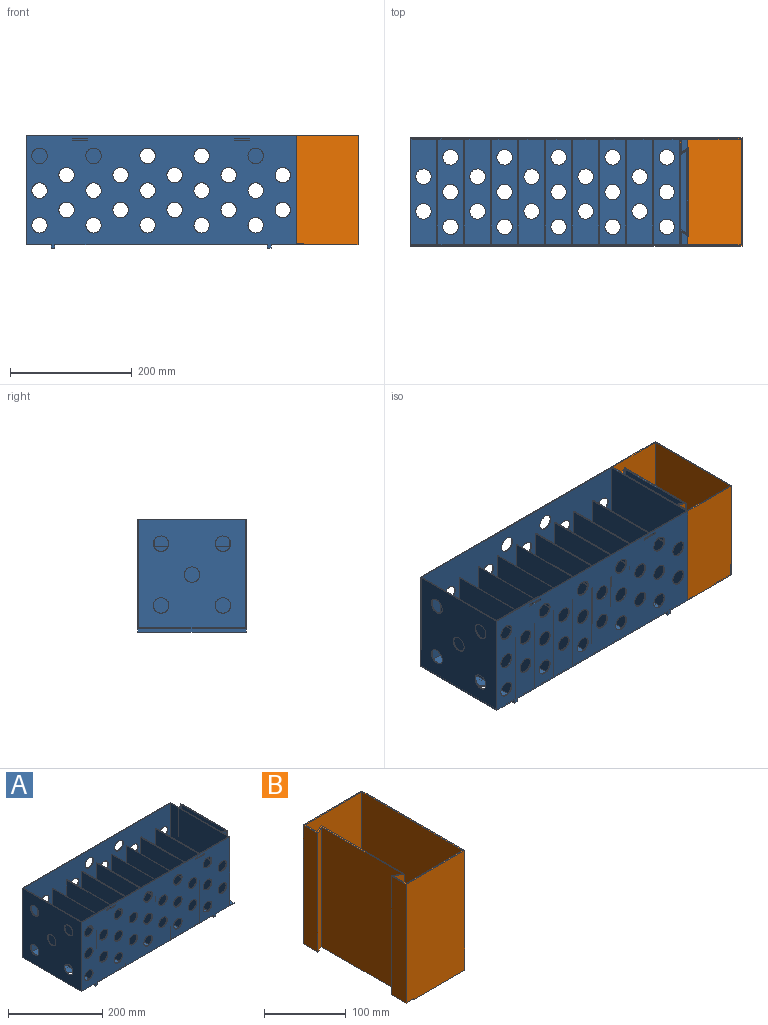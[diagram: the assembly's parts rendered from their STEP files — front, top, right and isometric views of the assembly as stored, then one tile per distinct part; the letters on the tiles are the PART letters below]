
ASSEMBLY  parts=2 mates=1
PART A: 151 faces, bbox 457.2x177.8x185.7 mm
  f0: plane 457.2x185.74mm, normal (0,-1,0), area 67009.6mm2, adj f20,f31,f32,f34,f59,f62,f63,f64
  f1: plane 441.33x177.8mm, normal (0,1,0), area 63733.4mm2, adj f2,f3,f4,f5,f6,f7,f8,f9
  f2: plane 174.63x133.35mm, normal (-1,0,0), area 23286.2mm2, adj f1,f61,f69,f134
  f3: plane 174.63x133.35mm, normal (-1,0,0), area 23286.2mm2, adj f1,f22,f69,f136
  f4: plane 174.63x133.35mm, normal (1,0,0), area 23286.2mm2, adj f1,f22,f69,f135
  f5: plane 174.63x133.35mm, normal (-1,0,0), area 23286.2mm2, adj f1,f23,f69,f138
  f6: plane 174.63x133.35mm, normal (1,0,0), area 23286.2mm2, adj f1,f23,f69,f137
  f7: plane 174.63x133.35mm, normal (-1,0,0), area 23286.2mm2, adj f1,f24,f69,f140
  f8: plane 174.63x133.35mm, normal (1,0,0), area 23286.2mm2, adj f1,f24,f69,f139
  f9: plane 174.63x133.35mm, normal (-1,0,0), area 23286.2mm2, adj f1,f25,f69,f142
  f10: plane 174.63x133.35mm, normal (1,0,0), area 23286.2mm2, adj f1,f25,f69,f141
  f11: plane 174.63x133.35mm, normal (1,0,0), area 23286.2mm2, adj f1,f26,f69,f142
  f12: plane 174.63x133.35mm, normal (-1,0,0), area 23286.2mm2, adj f1,f27,f69,f141
  f13: plane 174.63x133.35mm, normal (1,0,0), area 23286.2mm2, adj f1,f27,f69,f140
  f14: plane 174.63x133.35mm, normal (-1,0,0), area 23286.2mm2, adj f1,f28,f69,f139
  f15: plane 174.63x133.35mm, normal (1,0,0), area 23286.2mm2, adj f1,f28,f69,f138
  f16: plane 174.63x133.35mm, normal (-1,0,0), area 23286.2mm2, adj f1,f29,f69,f137
  f17: plane 174.63x133.35mm, normal (1,0,0), area 23286.2mm2, adj f1,f29,f69,f136
  f18: plane 174.63x133.35mm, normal (-1,0,0), area 23286.2mm2, adj f1,f30,f69,f135
  f19: plane 174.63x133.35mm, normal (1,0,0), area 23286.2mm2, adj f1,f30,f69,f134
  f20: plane 25.4x12.7mm, normal (0,0,1), area 282.3mm2, adj f0,f59,f76,f77
  f21: plane 25.4x12.7mm, normal (0,0,1), area 282.3mm2, adj f33,f59,f74,f75
  f22: plane 174.63x42.7mm, normal (0,0,1), area 6443.7mm2, adj f1,f3,f4,f36,f37,f69
  f23: plane 174.63x42.7mm, normal (0,0,1), area 6443.7mm2, adj f1,f5,f6,f38,f39,f69
  f24: plane 174.63x42.7mm, normal (0,0,1), area 6443.7mm2, adj f1,f7,f8,f40,f41,f69
  f25: plane 174.63x42.7mm, normal (0,0,1), area 6443.7mm2, adj f1,f9,f10,f42,f43,f69
  f26: plane 174.63x42.7mm, normal (0,0,1), area 5937mm2, adj f1,f11,f56,f57,f58,f69,f70
  f27: plane 174.63x42.7mm, normal (0,0,1), area 5937mm2, adj f1,f12,f13,f53,f54,f55,f69
  f28: plane 174.63x42.7mm, normal (0,0,1), area 5937mm2, adj f1,f14,f15,f50,f51,f52,f69
  f29: plane 174.63x42.7mm, normal (0,0,1), area 5937mm2, adj f1,f16,f17,f47,f48,f49,f69
  f30: plane 174.63x42.7mm, normal (0,0,1), area 5937mm2, adj f1,f18,f19,f44,f45,f46,f69
  f31: plane 349.25x177.8mm, normal (0,0,-1), area 51962.5mm2, adj f0,f33,f36,f37,f38,f39,f40,f41
  f32: plane 177.8x53.98mm, normal (0,0,-1), area 8076.6mm2, adj f0,f33,f56,f57,f58,f59,f64
  f33: plane 457.2x185.74mm, normal (0,1,0), area 68691mm2, adj f21,f31,f32,f34,f59,f62,f63,f64
  f34: plane 179.39x177.8mm, normal (-1,0,0), area 29361.6mm2, adj f0,f33,f62,f80,f129,f130,f131,f132
  f35: cylinder r=12.7mm len=25.4mm, axis (0,0,-1), area 126.7mm2, adj f61,f62
  f36: cylinder r=12.7mm len=25.4mm, axis (0,0,-1), area 126.7mm2, adj f22,f31
  f37: cylinder r=12.7mm len=25.4mm, axis (0,0,-1), area 126.7mm2, adj f22,f31
  f38: cylinder r=12.7mm len=25.4mm, axis (0,0,-1), area 126.7mm2, adj f23,f31
  f39: cylinder r=12.7mm len=25.4mm, axis (0,0,-1), area 126.7mm2, adj f23,f31
  f40: cylinder r=12.7mm len=25.4mm, axis (0,0,-1), area 126.7mm2, adj f24,f31
  f41: cylinder r=12.7mm len=25.4mm, axis (0,0,-1), area 126.7mm2, adj f24,f31
  f42: cylinder r=12.7mm len=25.4mm, axis (0,0,-1), area 126.7mm2, adj f25,f31
  f43: cylinder r=12.7mm len=25.4mm, axis (0,0,-1), area 126.7mm2, adj f25,f31
  f44: cylinder r=12.7mm len=25.4mm, axis (0,0,-1), area 126.7mm2, adj f30,f31
  f45: cylinder r=12.7mm len=25.4mm, axis (0,0,-1), area 126.7mm2, adj f30,f31
  f46: cylinder r=12.7mm len=25.4mm, axis (0,0,-1), area 126.7mm2, adj f30,f31
  f47: cylinder r=12.7mm len=25.4mm, axis (0,0,-1), area 126.7mm2, adj f29,f31
  f48: cylinder r=12.7mm len=25.4mm, axis (0,0,-1), area 126.7mm2, adj f29,f31
  f49: cylinder r=12.7mm len=25.4mm, axis (0,0,-1), area 126.7mm2, adj f29,f31
  f50: cylinder r=12.7mm len=25.4mm, axis (0,0,-1), area 126.7mm2, adj f28,f31
  f51: cylinder r=12.7mm len=25.4mm, axis (0,0,-1), area 126.7mm2, adj f28,f31
  f52: cylinder r=12.7mm len=25.4mm, axis (0,0,-1), area 126.7mm2, adj f28,f31
  f53: cylinder r=12.7mm len=25.4mm, axis (0,0,-1), area 126.7mm2, adj f27,f31
  f54: cylinder r=12.7mm len=25.4mm, axis (0,0,-1), area 126.7mm2, adj f27,f31
  f55: cylinder r=12.7mm len=25.4mm, axis (0,0,-1), area 126.7mm2, adj f27,f31
  f56: cylinder r=12.7mm len=25.4mm, axis (0,0,-1), area 126.7mm2, adj f26,f32
  f57: cylinder r=12.7mm len=25.4mm, axis (0,0,-1), area 126.7mm2, adj f26,f32
  f58: cylinder r=12.7mm len=25.4mm, axis (0,0,-1), area 126.7mm2, adj f26,f32
  f59: plane 179.39x177.8mm, normal (1,0,0), area 25120.9mm2, adj f0,f20,f21,f32,f33,f74,f77,f80
  f60: cylinder r=12.7mm len=25.4mm, axis (0,0,-1), area 126.7mm2, adj f61,f62
  f61: plane 174.63x42.7mm, normal (0,0,1), area 6443.7mm2, adj f1,f2,f35,f60,f69,f79
  f62: plane 177.8x41.28mm, normal (0,0,-1), area 6325.3mm2, adj f0,f33,f34,f35,f60,f66
  f63: plane 177.8x6.35mm, normal (-1,0,0), area 1129mm2, adj f0,f31,f33,f65
  f64: plane 177.8x6.35mm, normal (1,0,0), area 1129mm2, adj f0,f32,f33,f65
  f65: plane 177.8x6.35mm, normal (0,0,-1), area 1129mm2, adj f0,f33,f63,f64
  f66: plane 177.8x6.35mm, normal (-1,0,0), area 1129mm2, adj f0,f33,f62,f68
  f67: plane 177.8x6.35mm, normal (1,0,0), area 1129mm2, adj f0,f31,f33,f68
  f68: plane 177.8x6.35mm, normal (0,0,-1), area 1129mm2, adj f0,f33,f66,f67
  f69: plane 441.33x177.8mm, normal (0,-1,0), area 65414.8mm2, adj f2,f3,f4,f5,f6,f7,f8,f9
  f70: plane 177.8x174.63mm, normal (-1,0,0), area 31048.3mm2, adj f1,f26,f69,f80
  f71: plane 177.8x123.45mm, normal (1,0,0), area 21949.5mm2, adj f72,f78,f80,f81
  f72: plane 177.8x11.11mm, normal (0.45,-0.89,0), area 2209mm2, adj f71,f73,f80,f81
  f73: plane 177.8x134.56mm, normal (-1,0,0), area 23925.3mm2, adj f72,f78,f80,f81
  f74: plane 177.8x12.7mm, normal (-0.45,0.89,0), area 2524.6mm2, adj f21,f59,f75,f80
  f75: plane 177.8x25.4mm, normal (1,0,0), area 4516.1mm2, adj f21,f33,f74,f80
  f76: plane 177.8x25.4mm, normal (1,0,0), area 4516.1mm2, adj f0,f20,f77,f80
  f77: plane 177.8x12.7mm, normal (-0.45,-0.89,0), area 2524.6mm2, adj f20,f59,f76,f80
  f78: plane 177.8x11.11mm, normal (0.45,0.89,0), area 2209mm2, adj f71,f73,f80,f81
  f79: plane 177.8x174.63mm, normal (1,0,0), area 28514.8mm2, adj f1,f61,f69,f80,f129,f130,f131,f132
  f80: plane 457.2x177.8mm, normal (0,0,1), area 2225.7mm2, adj f0,f1,f33,f34,f59,f69,f70,f71
  f81: plane 134.56x11.11mm, normal (0,0,1), area 1433.6mm2, adj f71,f72,f73,f78
  f82: cylinder r=12.7mm len=25.4mm, axis (0,-1,0), area 126.7mm2, adj f33,f69
  f83: cylinder r=12.7mm len=25.4mm, axis (0,-1,0), area 126.7mm2, adj f33,f69
  f84: cylinder r=12.7mm len=25.4mm, axis (0,-1,0), area 126.7mm2, adj f33,f69
  f85: cylinder r=12.7mm len=25.4mm, axis (0,-1,0), area 126.7mm2, adj f33,f69
  f86: cylinder r=12.7mm len=25.4mm, axis (0,-1,0), area 126.7mm2, adj f33,f69
  f87: cylinder r=12.7mm len=25.4mm, axis (0,-1,0), area 126.7mm2, adj f33,f69
  f88: cylinder r=12.7mm len=25.4mm, axis (0,-1,0), area 126.7mm2, adj f33,f69
  f89: cylinder r=12.7mm len=25.4mm, axis (0,-1,0), area 126.7mm2, adj f33,f69
  f90: cylinder r=12.7mm len=25.4mm, axis (0,-1,0), area 126.7mm2, adj f33,f69
  f91: cylinder r=12.7mm len=25.4mm, axis (0,-1,0), area 126.7mm2, adj f33,f69
  f92: cylinder r=12.7mm len=25.4mm, axis (0,-1,0), area 126.7mm2, adj f33,f69
  f93: cylinder r=12.7mm len=25.4mm, axis (0,-1,0), area 126.7mm2, adj f33,f69
  f94: cylinder r=12.7mm len=25.4mm, axis (0,-1,0), area 126.7mm2, adj f33,f69
  f95: cylinder r=12.7mm len=25.4mm, axis (0,-1,0), area 126.7mm2, adj f33,f69
  f96: cylinder r=12.7mm len=25.4mm, axis (0,-1,0), area 126.7mm2, adj f33,f69
  f97: cylinder r=12.7mm len=25.4mm, axis (0,-1,0), area 126.7mm2, adj f33,f69
  f98: cylinder r=12.7mm len=25.4mm, axis (0,-1,0), area 126.7mm2, adj f33,f69
  f99: cylinder r=12.7mm len=25.4mm, axis (0,-1,0), area 126.7mm2, adj f33,f69
  f100: cylinder r=12.7mm len=25.4mm, axis (0,-1,0), area 126.7mm2, adj f33,f69
  f101: cylinder r=12.7mm len=25.4mm, axis (0,-1,0), area 126.7mm2, adj f33,f69
  f102: cylinder r=12.7mm len=25.4mm, axis (0,-1,0), area 126.7mm2, adj f0,f1
  f103: cylinder r=12.7mm len=25.4mm, axis (0,-1,0), area 126.7mm2, adj f0,f1
  f104: cylinder r=12.7mm len=25.4mm, axis (0,-1,0), area 126.7mm2, adj f0,f1
  f105: cylinder r=12.7mm len=25.4mm, axis (0,-1,0), area 126.7mm2, adj f0,f1
  f106: cylinder r=12.7mm len=25.4mm, axis (0,-1,0), area 126.7mm2, adj f0,f1
  f107: cylinder r=12.7mm len=25.4mm, axis (0,-1,0), area 126.7mm2, adj f0,f1
  f108: cylinder r=12.7mm len=25.4mm, axis (0,-1,0), area 126.7mm2, adj f0,f1
  f109: cylinder r=12.7mm len=25.4mm, axis (0,-1,0), area 126.7mm2, adj f0,f1
  f110: cylinder r=12.7mm len=25.4mm, axis (0,-1,0), area 126.7mm2, adj f0,f1
  f111: cylinder r=12.7mm len=25.4mm, axis (0,-1,0), area 126.7mm2, adj f0,f1
  f112: cylinder r=12.7mm len=25.4mm, axis (0,-1,0), area 126.7mm2, adj f0,f1
  f113: cylinder r=12.7mm len=25.4mm, axis (0,-1,0), area 126.7mm2, adj f0,f1
  f114: cylinder r=12.7mm len=25.4mm, axis (0,-1,0), area 126.7mm2, adj f0,f1
  f115: cylinder r=12.7mm len=25.4mm, axis (0,-1,0), area 126.7mm2, adj f0,f1
  f116: cylinder r=12.7mm len=25.4mm, axis (0,-1,0), area 126.7mm2, adj f0,f1
  f117: cylinder r=12.7mm len=25.4mm, axis (0,-1,0), area 126.7mm2, adj f0,f1
  f118: cylinder r=12.7mm len=25.4mm, axis (0,-1,0), area 126.7mm2, adj f0,f1
  f119: cylinder r=12.7mm len=25.4mm, axis (0,-1,0), area 126.7mm2, adj f0,f1
  f120: cylinder r=12.7mm len=25.4mm, axis (0,-1,0), area 126.7mm2, adj f0,f1
  f121: cylinder r=12.7mm len=25.4mm, axis (0,-1,0), area 126.7mm2, adj f0,f1
  f122: cylinder r=12.7mm len=25.4mm, axis (0,-1,0), area 126.7mm2, adj f0,f1
  f123: cylinder r=12.7mm len=25.4mm, axis (0,-1,0), area 126.7mm2, adj f0,f1
  f124: cylinder r=12.7mm len=25.4mm, axis (0,-1,0), area 126.7mm2, adj f33,f69
  f125: cylinder r=12.7mm len=25.4mm, axis (0,-1,0), area 126.7mm2, adj f33,f69
  f126: cylinder r=12.7mm len=25.4mm, axis (0,-1,0), area 126.7mm2, adj f0,f1
  f127: cylinder r=12.7mm len=25.4mm, axis (0,-1,0), area 126.7mm2, adj f0,f1
  f128: cylinder r=12.7mm len=25.4mm, axis (0,-1,0), area 126.7mm2, adj f0,f1
  f129: cylinder r=12.7mm len=25.4mm, axis (-1,0,0), area 126.7mm2, adj f34,f79
  f130: cylinder r=12.7mm len=25.4mm, axis (-1,0,0), area 126.7mm2, adj f34,f79
  f131: cylinder r=12.7mm len=25.4mm, axis (-1,0,0), area 126.7mm2, adj f34,f79
  f132: cylinder r=12.7mm len=25.4mm, axis (-1,0,0), area 126.7mm2, adj f34,f79
  f133: cylinder r=12.7mm len=25.4mm, axis (-1,0,0), area 126.7mm2, adj f34,f79
  f134: plane 174.63x1.59mm, normal (0,0,1), area 277.2mm2, adj f1,f2,f19,f69
  f135: plane 174.63x1.59mm, normal (0,0,1), area 277.2mm2, adj f1,f4,f18,f69
  f136: plane 174.63x1.59mm, normal (0,0,1), area 277.2mm2, adj f1,f3,f17,f69
  f137: plane 174.63x1.59mm, normal (0,0,1), area 277.2mm2, adj f1,f6,f16,f69
  f138: plane 174.63x1.59mm, normal (0,0,1), area 277.2mm2, adj f1,f5,f15,f69
  f139: plane 174.63x1.59mm, normal (0,0,1), area 277.2mm2, adj f1,f8,f14,f69
  f140: plane 174.63x1.59mm, normal (0,0,1), area 277.2mm2, adj f1,f7,f13,f69
  f141: plane 174.63x1.59mm, normal (0,0,1), area 277.2mm2, adj f1,f10,f12,f69
  f142: plane 174.63x1.59mm, normal (0,0,1), area 277.2mm2, adj f1,f9,f11,f69
  f143: plane 25.4x1.59mm, normal (0,0,-1), area 40.3mm2, adj f0,f1,f144,f146
  f144: plane 3.18x1.59mm, normal (1,0,0), area 5mm2, adj f0,f1,f143,f145
  f145: plane 25.4x1.59mm, normal (0,0,1), area 40.3mm2, adj f0,f1,f144,f146
  f146: plane 3.18x1.59mm, normal (-1,0,0), area 5mm2, adj f0,f1,f143,f145
  f147: plane 3.18x1.59mm, normal (-1,0,0), area 5mm2, adj f0,f1,f148,f150
  f148: plane 25.4x1.59mm, normal (0,0,-1), area 40.3mm2, adj f0,f1,f147,f149
  f149: plane 3.18x1.59mm, normal (1,0,0), area 5mm2, adj f0,f1,f148,f150
  f150: plane 25.4x1.59mm, normal (0,0,1), area 40.3mm2, adj f0,f1,f147,f149
PART B: 21 faces, bbox 101.6x177.8x179.4 mm
  f0: plane 174.63x87.31mm, normal (0,0,1), area 15018.3mm2, adj f4,f12,f13,f14,f16,f17,f18
  f1: plane 179.39x101.6mm, normal (0,-1,0), area 18205.6mm2, adj f2,f4,f5,f7,f11,f20
  f2: plane 179.39x177.8mm, normal (1,0,0), area 31895.1mm2, adj f1,f3,f5,f20
  f3: plane 179.39x101.6mm, normal (0,1,0), area 18205.6mm2, adj f2,f4,f5,f6,f8,f20
  f4: plane 179.39x177.8mm, normal (-1,0,0), area 25120.9mm2, adj f0,f1,f3,f5,f6,f7,f9,f10
  f5: plane 177.8x88.9mm, normal (0,0,-1), area 15806.4mm2, adj f1,f2,f3,f4
  f6: plane 25.4x12.7mm, normal (0,0,-1), area 77.1mm2, adj f3,f4,f8,f9,f12,f18,f19
  f7: plane 25.4x12.7mm, normal (0,0,-1), area 77.1mm2, adj f1,f4,f10,f11,f14,f15,f16
  f8: plane 177.8x25.4mm, normal (-1,0,0), area 4516.1mm2, adj f3,f6,f9,f20
  f9: plane 177.8x12.7mm, normal (0.45,-0.89,0), area 2524.6mm2, adj f4,f6,f8,f20
  f10: plane 177.8x12.7mm, normal (0.45,0.89,0), area 2524.6mm2, adj f4,f7,f11,f20
  f11: plane 177.8x25.4mm, normal (-1,0,0), area 4516.1mm2, adj f1,f7,f10,f20
  f12: plane 177.8x98.43mm, normal (0,-1,0), area 17500mm2, adj f0,f6,f13,f19,f20
  f13: plane 177.8x174.63mm, normal (-1,0,0), area 31048.3mm2, adj f0,f12,f14,f20
  f14: plane 177.8x98.43mm, normal (0,1,0), area 17500mm2, adj f0,f7,f13,f15,f20
  f15: plane 177.8x21.24mm, normal (1,0,0), area 3777.2mm2, adj f7,f14,f16,f20
  f16: plane 177.8x12.7mm, normal (-0.45,-0.89,0), area 2524.6mm2, adj f0,f7,f15,f17,f20
  f17: plane 177.8x144.84mm, normal (1,0,0), area 25752.1mm2, adj f0,f16,f18,f20
  f18: plane 177.8x12.7mm, normal (-0.45,0.89,0), area 2524.6mm2, adj f0,f6,f17,f19,f20
  f19: plane 177.8x21.24mm, normal (1,0,0), area 3777.2mm2, adj f6,f12,f18,f20
  f20: plane 177.8x101.6mm, normal (0,0,1), area 942.3mm2, adj f1,f2,f3,f4,f8,f9,f10,f11
PLACE A at identity fixed
PLACE B t=(444.5,0,1.59)mm
MATE fastened A.f80 <-> B.f20  axis (0,0,-1) through (444.5,0,179.39)mm
